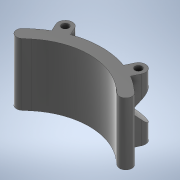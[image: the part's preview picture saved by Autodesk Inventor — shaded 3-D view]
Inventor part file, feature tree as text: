
AUTODESK INVENTOR PART (.ipt)
format: ipt  version: 2020 (Build 240168000, 168)  size: 424,448 bytes
history: native  units: mm
features: sketch x5, extrude x4, projected_geometry x2, other x1, sweep x1
ambient origin geometry x8: Origin, YZ Plane, XZ Plane, XY Plane, X Axis, Y Axis, Z Axis, Center Point
bodies: Body1 (feature_tree)
feature tree (13):
  other  "Твердое тело1"
  extrude  "Выдавливание1"  Depth=35.0mm TaperAngle=0.0deg
  sketch  "Эскиз2"
  extrude  "Выдавливание2"  Depth=4.0mm
  sweep  "Сдвиг1"
  extrude  "Выдавливание5"  Depth=8.0mm
  extrude  "Выдавливание6"  Depth=35.0mm TaperAngle=0.0deg
  sketch  "Эскиз1"
  sketch  "Эскиз3"
  projected_geometry  "Спроецированная петля1"
  projected_geometry  "Спроецированная петля2"
  sketch  "3D эскиз1"
  sketch  "Эскиз4"
